# Revit family: NBS_HeatraeSadia_StrgWtrHtrsElctrc_Hotflo
name_source: partatom
category: Plumbing Fixtures
revit_build: Autodesk Revit 2014 (Build: 20130709_2115(x64)
units: mm (PartAtom-declared; Revit-internal decimal feet)

## types (2) — shared parameters
Accessories = Accessory pack U1 (95:970:352), Accessory pack U3 (95:970:354), Accessory pack U5 (95:970:356), Accessory pack U6 (95:970:359), Accessory pack U7 (95:970:360)
Arrangement = Single point – mains supply
AssetType = Fixed
CW Connection = No
CasingFinish = White stove enamel
Color = White
Connections = 15 mm copper tail ends, fitted with 1 m of three core cable
Controls = For use with standard tap or mixer
Depth = 252 mm  [stored 0.826772 ft]
Description = Unvented point of use storage water heater
DurationUnit = year
Features = Element ‘on’ indicator, no anode to inspect or replace, suitable for use with any standard tap or mixer
Fixing = Floor or wall fixed
FlowRate = To suit draw off requirements
HW Connection = No
HeatTransferSurfaceArea = 0
IPCode = IPX4
IfcExportAs = IfcBoilerType
IfcExportType = WATER
IsWaterStorageHeater = Yes
KeyHoleSlotHeight = 360 mm  [stored 1.1811 ft]
ManufacturerName = Heatrae Sadia
ManufacturerURL = www.heatraesadia.com
Material = Outer casing: Plastic top moulding with steel base and centre section; Water container: Replaceable heavy gauge copper; Heat unit: Replaceable rod-type element sheathed in corrosion resistant alloy
NBSCertification = http://www.nationalbimlibrary.com
NBSDescription = Storage water heaters, electric
NBSReference = 90-15-35/440
NominalLength = 252 mm  [stored 0.826772 ft]
NominalWidth = 267 mm  [stored 0.875984 ft]
OutletTemperatureRange = 10, 70
PartialLoadEfficiencyCurves = 0
PressureRating = 0
ProductInformation = www.heatraesadia.com/docs/POU_unvented_water_heating_brochure.pdf
Rating = 2.2 kW
SafetyFeatures = Pressure relief valve set to open at 6 bar, resettable over temperature cut-out
StorageWaterHeaterMaterial = NBS_Concept
ThermalInsulation = CFC/HCFC free (ODP zero) flame-retardant expanded polyurethane
ThirdPartyCertification = BEAB approved, Kiwa approved
Uniclass2 = 90-90-46/428
Uniclass2015Description = Electric storage water heaters
Uniclass2015Reference = Pr_60_60_96_28
Uniclass2015Version = Products v1.1
Version = 1
WarrantyDurationParts = 2
WarrantyDurationUnit = year
WarrantyStartDate = 1900-12-31T23:59:59
WaterInletTemperatureRange = 0
Width = 267 mm  [stored 0.875984 ft]
zero-valued in all types: HeatOutput, NominalEfficiency, NominalEnergyConsumption, NominalPartLoadRatio

## per-type parameters (varying)
| type | BIMObjectName | BodyHeight | Height | ModelNumber | ModelReference | Name | NominalHeight | Size | WaterStorageCapacity | Weight |
| Hotflo10 | NBS_HeatraeSadia_StorageWaterHeatersElectric_Hotflo10 | 457 mm | 500 mm  [stored 1.64042 ft] | 95:050:148 | Hotflo 10 | StorageWaterHeatersElectric_Hotflo10_HeatraeSadia | 500 mm  [stored 1.64042 ft] | 500 x 267 x 252 mm | 10 | 16.5 |
| Hotflo15 | NBS_HeatraeSadia_StorageWaterHeatersElectric_Hotflo15 | 613 mm  [stored 2.01115 ft] | 656 mm  [stored 2.15223 ft] | 95:050:149 | Hotflo 15 | StorageWaterHeatersElectric_Hotflo15_HeatraeSadia | 656 mm  [stored 2.15223 ft] | 656 x 267 x 252 mm | 15 | 23.4 |

note: [stored X ft] marks values corroborated as IEEE doubles in the binary element streams (Revit-internal decimal feet)

## geometry (parser evidence)
native form markers: Blend x13, Sweep x1
no freeform markers — native parametric forms only
